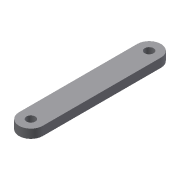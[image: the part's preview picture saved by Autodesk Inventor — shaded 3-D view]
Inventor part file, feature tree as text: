
AUTODESK INVENTOR PART (.ipt)
format: ipt  version: 2018 (Build 220112000, 112)  size: 84,480 bytes
history: native  units: mm
features: extrude x1, sketch x1
ambient origin geometry x8: Origin, YZ Plane, XZ Plane, XY Plane, X Axis, Y Axis, Z Axis, Center Point
bodies: Solid1 (feature_tree)
feature tree (2):
  extrude  "Extrusion1"  Depth=8.0mm
  sketch  "Sketch1"  dims[d0=3.0mm d1=8.0mm d2=40.0mm d3=3.0mm d4=8.0mm d5=3.0mm d6=0.0mm]
